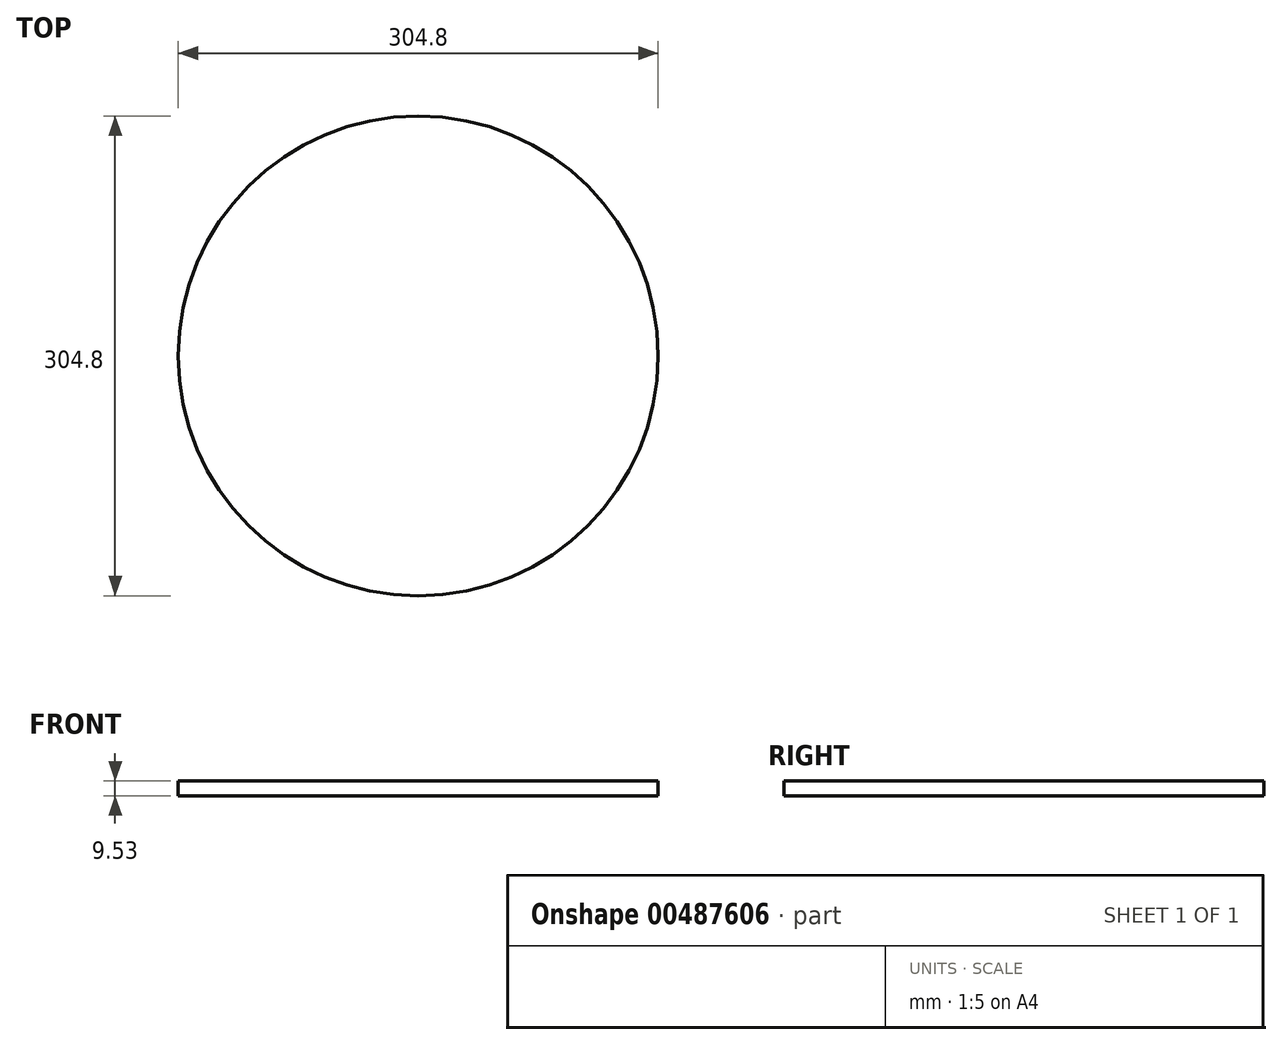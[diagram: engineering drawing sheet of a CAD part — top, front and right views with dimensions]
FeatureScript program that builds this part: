
annotation { "Feature Type Name" : "Feature", "Feature Type Description" : "" }
export const myFeature = defineFeature(function(context is Context, id is Id, definition is map)
    precondition{}
    {
        {
            var Q0;
            Q0=qCreatedBy(makeId("Top.planeOp"),FACE);
            var sketch = newSketch(context, id + "F0", { "sketchPlane" : qUnion([Q0])});
            skCircle(sketch, "E0", {"center": v(0, 0) * mm, "radius": 152.4 * mm});
            skSolve(sketch);
        }
        {
            var Q0;
            Q0=makeQuery(id+"F0.imprint","IMPRINT",FACE,{"disambiguationData":[TD([[makeQuery(id+"F0.imprint","IMPRINT",EDGE,{"derivedFrom":sQuery(id+"F0.wireOp",EDGE,"E0")}),1.0]])]});
            extrude(context, id + "F1", {"entities" : qUnion([Q0]), "depth" : 9.52 * mm});
        }
    });
